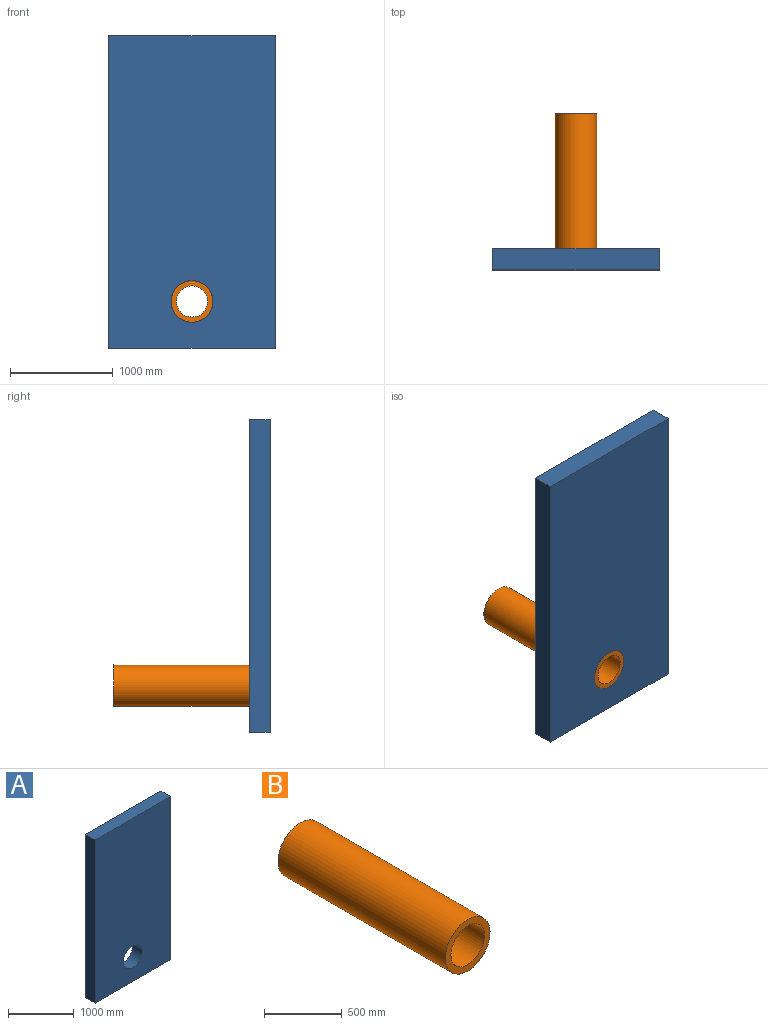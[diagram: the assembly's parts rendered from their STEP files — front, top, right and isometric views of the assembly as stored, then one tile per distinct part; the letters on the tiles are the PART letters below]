
ASSEMBLY  parts=2 mates=1
PART A: 7 faces, bbox 1625.5x203.3x3048 mm
  f0: plane 1625.5x203.3mm, normal (0,0,1), area 330466.4mm2, adj f1,f3,f4,f5
  f1: plane 3048x203.3mm, normal (-1,0,0), area 619663.3mm2, adj f0,f2,f4,f5
  f2: plane 1625.5x203.3mm, normal (0,0,-1), area 330466.4mm2, adj f1,f3,f4,f5
  f3: plane 3048x203.3mm, normal (1,0,0), area 619663.3mm2, adj f0,f2,f4,f5
  f4: plane 3048x1625.5mm, normal (0,-1,0), area 4824802mm2, adj f0,f1,f2,f3,f6
  f5: plane 3048x1625.5mm, normal (0,1,0), area 4824802mm2, adj f0,f1,f2,f3,f6
  f6: cylinder r=203.2mm len=406.4mm, axis (0,1,0), area 259563.9mm2, adj f4,f5
PART B: 4 faces, bbox 406.6x1524x406.6 mm
  f0: plane 406.6x406.6mm, normal (0,-1,0), area 56881mm2, adj f2,f3
  f1: plane 406.6x406.6mm, normal (0,1,0), area 56881mm2, adj f2,f3
  f2: cylinder r=203.3mm len=1524mm, axis (0,-1,0), area 1946729.6mm2, adj f0,f1
  f3: cylinder r=152.4mm len=1524mm, axis (0,-1,0), area 1459317.5mm2, adj f0,f1
PLACE A at identity
PLACE B t=(0,-203.3,-1066.8)mm
MATE slider B.f2 <-> A.f6  axis (0,-1,0) through (0,-203.3,-1066.8)mm
